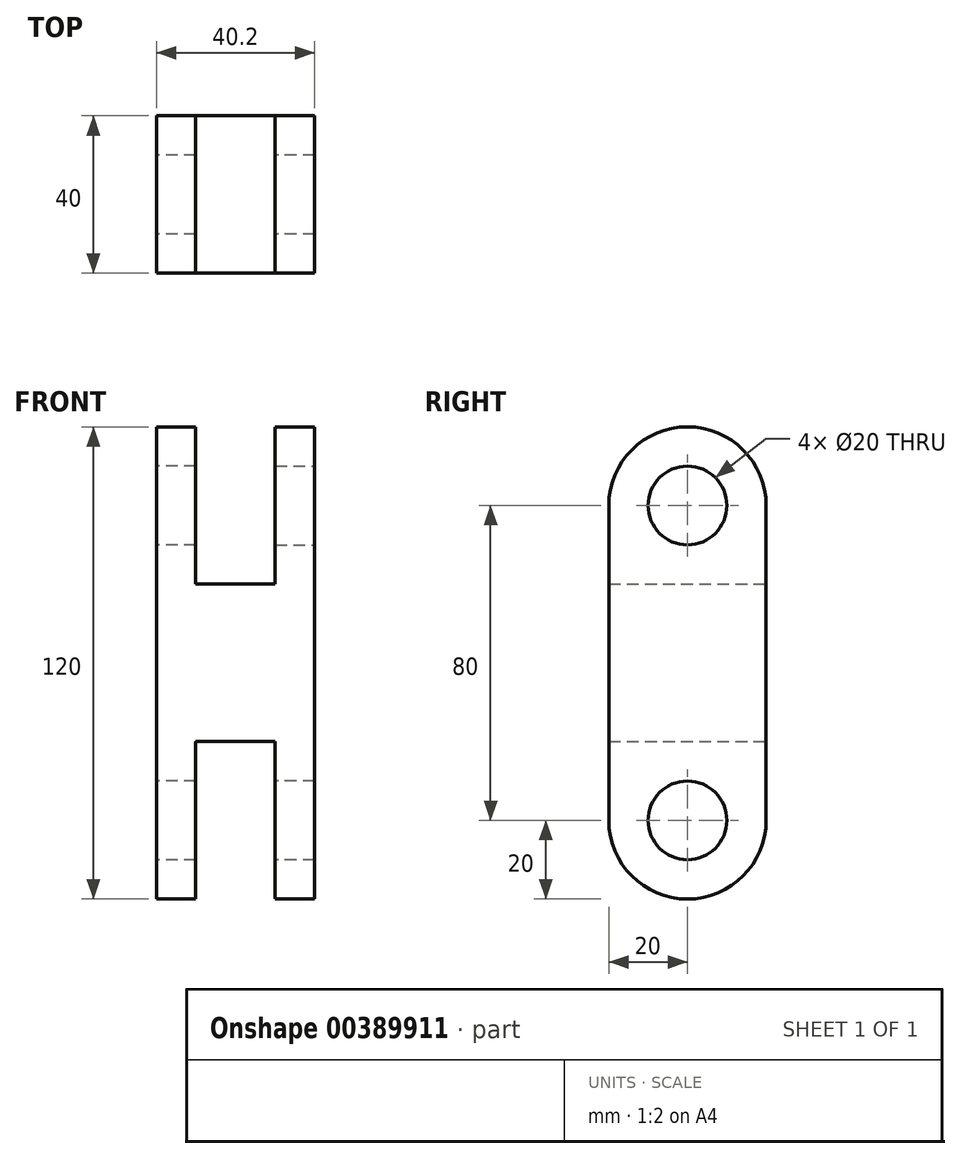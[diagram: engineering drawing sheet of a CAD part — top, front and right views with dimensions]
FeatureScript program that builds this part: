
annotation { "Feature Type Name" : "Feature", "Feature Type Description" : "" }
export const myFeature = defineFeature(function(context is Context, id is Id, definition is map)
    precondition{}
    {
        {
            var Q0;
            Q0=qCreatedBy(makeId("Right.planeOp"),FACE);
            var sketch = newSketch(context, id + "F0", { "sketchPlane" : qUnion([Q0])});
            skLineSegment(sketch, "E0.bottom", {"start": v(-20, 40) * mm, "end": v(20, 40) * mm});
            skLineSegment(sketch, "E0.top", {"start": v(-20, -40) * mm, "end": v(20, -40) * mm});
            skLineSegment(sketch, "E0.left", {"start": v(-20, 40) * mm, "end": v(-20, -40) * mm});
            skLineSegment(sketch, "E0.right", {"start": v(20, 40) * mm, "end": v(20, -40) * mm});
            skPoint(sketch, "E0.middle", {"position": v(0, 0) * mm});
            skSolve(sketch);
        }
        {
            var Q0;
            Q0 = qSketchRegion(id + "F0", true);
            extrude(context, id + "F1", {"entities" : qUnion([Q0]), "depth" : 20.1 * mm});
        }
        {
            var Q0;
            Q0=makeQuery(id+"F1.opExtrude","CAP_FACE",FACE,{"disambiguationData":[OSD([sQuery(id+"F0.wireOp",EDGE,"E0.bottom"),sQuery(id+"F0.wireOp",EDGE,"E0.top"),sQuery(id+"F0.wireOp",EDGE,"E0.left"),sQuery(id+"F0.wireOp",EDGE,"E0.right")])],"isStart":false});
            var sketch = newSketch(context, id + "F2", { "sketchPlane" : qUnion([Q0])});
            skLineSegment(sketch, "E1.bottom", {"start": v(-20, 40) * mm, "end": v(20, 40) * mm});
            skLineSegment(sketch, "E1.top", {"start": v(-20, 80) * mm, "end": v(20, 80) * mm});
            skLineSegment(sketch, "E1.left", {"start": v(-20, 40) * mm, "end": v(-20, 80) * mm});
            skLineSegment(sketch, "E1.right", {"start": v(20, 40) * mm, "end": v(20, 80) * mm});
            skSolve(sketch);
        }
        {
            var Q0;
            Q0 = qSketchRegion(id + "F2", true);
            extrude(context, id + "F3", {"entities" : qUnion([Q0]), "operationType" : NewBodyOperationType.ADD, "oppositeDirection" : true, "depth" : 10 * mm});
        }
        {
            var Q0;
            Q0=makeQuery(id+"F3.boolean.opBoolean","MERGE",FACE,{"derivedFrom":[makeQuery(id+"F1.opExtrude","CAP_FACE",FACE,{"disambiguationData":[OSD([sQuery(id+"F0.wireOp",EDGE,"E0.bottom"),sQuery(id+"F0.wireOp",EDGE,"E0.top"),sQuery(id+"F0.wireOp",EDGE,"E0.left"),sQuery(id+"F0.wireOp",EDGE,"E0.right")])],"isStart":false}),makeQuery(id+"F3.opExtrude","CAP_FACE",FACE,{"disambiguationData":[OSD([sQuery(id+"F2.wireOp",EDGE,"E1.bottom"),sQuery(id+"F2.wireOp",EDGE,"E1.top"),sQuery(id+"F2.wireOp",EDGE,"E1.left"),sQuery(id+"F2.wireOp",EDGE,"E1.right")])],"isStart":true})]});
            var sketch = newSketch(context, id + "F4", { "sketchPlane" : qUnion([Q0])});
            skLineSegment(sketch, "E2", {"start": v(0, 80) * mm, "end": v(0, 60) * mm, "construction": true});
            skCircle(sketch, "E3", {"center": v(0, 60) * mm, "radius": 10 * mm});
            skSolve(sketch);
        }
        {
            var Q0;
            Q0 = qSketchRegion(id + "F4", true);
            extrude(context, id + "F5", {"entities" : qUnion([Q0]), "operationType" : NewBodyOperationType.REMOVE, "oppositeDirection" : true, "depth" : 10.1 * mm});
        }
        {
            var Q0;
            Q0=makeQuery(id+"F1.opExtrude","SWEPT_BODY",BODY,{"disambiguationData":[OSD([sQuery(id+"F0.wireOp",EDGE,"E0.bottom"),sQuery(id+"F0.wireOp",EDGE,"E0.top"),sQuery(id+"F0.wireOp",EDGE,"E0.left"),sQuery(id+"F0.wireOp",EDGE,"E0.right")])]});
            var Q1;
            Q1=makeQuery(id+"F1.opExtrude","CAP_FACE",FACE,{"disambiguationData":[OSD([sQuery(id+"F0.wireOp",EDGE,"E0.bottom"),sQuery(id+"F0.wireOp",EDGE,"E0.top"),sQuery(id+"F0.wireOp",EDGE,"E0.left"),sQuery(id+"F0.wireOp",EDGE,"E0.right")])],"isStart":true});
            mirror(context, id + "F6", {"operationType" : NewBodyOperationType.ADD, "entities" : qUnion([Q0]), "mirrorPlane" : qUnion([Q1])});
        }
        {
            var Q0;
            Q0=makeQuery(id+"F3.opExtrude","SWEPT_EDGE",EDGE,{"disambiguationData":[OSD([sQuery(id+"F2.wireOp",EDGE,"E1.top"),sQuery(id+"F2.wireOp",EDGE,"E1.right")])]});
            var Q1;
            Q1=makeQuery(id+"F3.opExtrude","SWEPT_EDGE",EDGE,{"disambiguationData":[OSD([sQuery(id+"F2.wireOp",EDGE,"E1.top"),sQuery(id+"F2.wireOp",EDGE,"E1.left")])]});
            var Q2;
            Q2=makeQuery(id+"F6.opPattern","COPY",EDGE,{"derivedFrom":makeQuery(id+"F3.opExtrude","SWEPT_EDGE",EDGE,{"disambiguationData":[OSD([sQuery(id+"F2.wireOp",EDGE,"E1.top"),sQuery(id+"F2.wireOp",EDGE,"E1.right")])]}),"instanceName":"1"});
            var Q3;
            Q3=makeQuery(id+"F6.opPattern","COPY",EDGE,{"derivedFrom":makeQuery(id+"F3.opExtrude","SWEPT_EDGE",EDGE,{"disambiguationData":[OSD([sQuery(id+"F2.wireOp",EDGE,"E1.top"),sQuery(id+"F2.wireOp",EDGE,"E1.left")])]}),"instanceName":"1"});
            fillet(context, id + "F7", {"entities" : qUnion([Q0, Q1, Q2, Q3]), "radius" : 20 * mm, "tangentPropagation" : true, "allowEdgeOverflow" : false});
        }
        {
            var Q0;
            Q0=makeQuery(id+"F6.opPattern","COPY",FACE,{"derivedFrom":makeQuery(id+"F3.boolean.opBoolean","MERGE",FACE,{"derivedFrom":[makeQuery(id+"F1.opExtrude","CAP_FACE",FACE,{"disambiguationData":[OSD([sQuery(id+"F0.wireOp",EDGE,"E0.bottom"),sQuery(id+"F0.wireOp",EDGE,"E0.top"),sQuery(id+"F0.wireOp",EDGE,"E0.left"),sQuery(id+"F0.wireOp",EDGE,"E0.right")])],"isStart":false}),makeQuery(id+"F3.opExtrude","CAP_FACE",FACE,{"disambiguationData":[OSD([sQuery(id+"F2.wireOp",EDGE,"E1.bottom"),sQuery(id+"F2.wireOp",EDGE,"E1.top"),sQuery(id+"F2.wireOp",EDGE,"E1.left"),sQuery(id+"F2.wireOp",EDGE,"E1.right")])],"isStart":true})]}),"instanceName":"1"});
            var sketch = newSketch(context, id + "F8", { "sketchPlane" : qUnion([Q0])});
            skLineSegment(sketch, "E4", {"start": v(0, -40) * mm, "end": v(0, -20) * mm, "construction": true});
            skPoint(sketch, "E4.endSnap0", {"position": v(0, -40) * mm});
            skCircle(sketch, "E5", {"center": v(0, -20) * mm, "radius": 10 * mm});
            skSolve(sketch);
        }
        {
            var Q0;
            Q0=makeQuery(id+"F8.imprint","IMPRINT",FACE,{"disambiguationData":[TD([[makeQuery(id+"F8.imprint","IMPRINT",EDGE,{"derivedFrom":sQuery(id+"F8.wireOp",EDGE,"E5")}),1.0]])]});
            extrude(context, id + "F9", {"entities" : qUnion([Q0]), "operationType" : NewBodyOperationType.REMOVE, "oppositeDirection" : true, "depth" : 80 * mm});
        }
        {
            var Q0;
            {var subQ0=makeQuery(id+"F3.boolean.opBoolean","MERGE",FACE,{"derivedFrom":[makeQuery(id+"F1.opExtrude","SWEPT_FACE",FACE,{"disambiguationData":[OSD([sQuery(id+"F0.wireOp",EDGE,"E0.right")])]}),makeQuery(id+"F3.opExtrude","SWEPT_FACE",FACE,{"disambiguationData":[OSD([sQuery(id+"F2.wireOp",EDGE,"E1.right")])]})]});Q0=makeQuery(id+"F6.boolean.opBoolean","MERGE",FACE,{"derivedFrom":[subQ0,makeQuery(id+"F6.opPattern","COPY",FACE,{"derivedFrom":subQ0,"instanceName":"1"})]});}
            var sketch = newSketch(context, id + "F10", { "sketchPlane" : qUnion([Q0])});
            skLineSegment(sketch, "E6.bottom", {"start": v(-10.1, -40) * mm, "end": v(10.1, -40) * mm});
            skLineSegment(sketch, "E6.top", {"start": v(-10.1, 0) * mm, "end": v(10.1, 0) * mm});
            skLineSegment(sketch, "E6.left", {"start": v(-10.1, -40) * mm, "end": v(-10.1, 0) * mm});
            skLineSegment(sketch, "E6.right", {"start": v(10.1, -40) * mm, "end": v(10.1, 0) * mm});
            skSolve(sketch);
        }
        {
            var Q0;
            Q0 = qSketchRegion(id + "F10", true);
            var Q1;
            {var subQ0=makeQuery(id+"F3.boolean.opBoolean","MERGE",FACE,{"derivedFrom":[makeQuery(id+"F1.opExtrude","SWEPT_FACE",FACE,{"disambiguationData":[OSD([sQuery(id+"F0.wireOp",EDGE,"E0.left")])]}),makeQuery(id+"F3.opExtrude","SWEPT_FACE",FACE,{"disambiguationData":[OSD([sQuery(id+"F2.wireOp",EDGE,"E1.left")])]})]});Q1=makeQuery(id+"F6.boolean.opBoolean","MERGE",FACE,{"derivedFrom":[subQ0,makeQuery(id+"F6.opPattern","COPY",FACE,{"derivedFrom":subQ0,"instanceName":"1"})]});}
            extrude(context, id + "F11", {"entities" : qUnion([Q0]), "operationType" : NewBodyOperationType.REMOVE, "endBound" : BoundingType.UP_TO_SURFACE, "oppositeDirection" : true, "endBoundEntityFace" : qUnion([Q1]), "depth" : 25 * mm});
        }
        {
            var Q0;
            {var subQ0=sQuery(id+"F0.wireOp",EDGE,"E0.top");var subQ2=sQuery(id+"F0.wireOp",EDGE,"E0.right");var subQ6=makeQuery(id+"F1.opExtrude","SWEPT_EDGE",EDGE,{"disambiguationData":[OSD([subQ0,subQ2])]});Q0=makeQuery(id+"F11.boolean.opBoolean","SPLIT",EDGE,{"disambiguationData":[TD([makeQuery(id+"F11.opExtrude","SWEPT_FACE",FACE,{"disambiguationData":[OSD([sQuery(id+"F10.wireOp",EDGE,"E6.right")])]})])],"derivedFrom":makeQuery(id+"F6.boolean.opBoolean","MERGE",EDGE,{"derivedFrom":[subQ6,makeQuery(id+"F6.opPattern","COPY",EDGE,{"derivedFrom":subQ6,"instanceName":"1"})]})});}
            var Q1;
            {var subQ0=sQuery(id+"F0.wireOp",EDGE,"E0.top");var subQ2=sQuery(id+"F0.wireOp",EDGE,"E0.left");var subQ6=makeQuery(id+"F1.opExtrude","SWEPT_EDGE",EDGE,{"disambiguationData":[OSD([subQ0,subQ2])]});Q1=makeQuery(id+"F11.boolean.opBoolean","SPLIT",EDGE,{"disambiguationData":[TD([makeQuery(id+"F11.opExtrude","SWEPT_FACE",FACE,{"disambiguationData":[OSD([sQuery(id+"F10.wireOp",EDGE,"E6.right")])]})])],"derivedFrom":makeQuery(id+"F6.boolean.opBoolean","MERGE",EDGE,{"derivedFrom":[subQ6,makeQuery(id+"F6.opPattern","COPY",EDGE,{"derivedFrom":subQ6,"instanceName":"1"})]})});}
            var Q2;
            {var subQ1=sQuery(id+"F0.wireOp",EDGE,"E0.right");var subQ2=sQuery(id+"F0.wireOp",EDGE,"E0.top");var subQ6=makeQuery(id+"F1.opExtrude","SWEPT_EDGE",EDGE,{"disambiguationData":[OSD([subQ2,subQ1])]});Q2=makeQuery(id+"F11.boolean.opBoolean","SPLIT",EDGE,{"disambiguationData":[TD([makeQuery(id+"F11.opExtrude","SWEPT_FACE",FACE,{"disambiguationData":[OSD([sQuery(id+"F10.wireOp",EDGE,"E6.left")])]})])],"derivedFrom":makeQuery(id+"F6.boolean.opBoolean","MERGE",EDGE,{"derivedFrom":[subQ6,makeQuery(id+"F6.opPattern","COPY",EDGE,{"derivedFrom":subQ6,"instanceName":"1"})]})});}
            var Q3;
            {var subQ1=sQuery(id+"F0.wireOp",EDGE,"E0.left");var subQ2=sQuery(id+"F0.wireOp",EDGE,"E0.top");var subQ6=makeQuery(id+"F1.opExtrude","SWEPT_EDGE",EDGE,{"disambiguationData":[OSD([subQ2,subQ1])]});Q3=makeQuery(id+"F11.boolean.opBoolean","SPLIT",EDGE,{"disambiguationData":[TD([makeQuery(id+"F11.opExtrude","SWEPT_FACE",FACE,{"disambiguationData":[OSD([sQuery(id+"F10.wireOp",EDGE,"E6.left")])]})])],"derivedFrom":makeQuery(id+"F6.boolean.opBoolean","MERGE",EDGE,{"derivedFrom":[subQ6,makeQuery(id+"F6.opPattern","COPY",EDGE,{"derivedFrom":subQ6,"instanceName":"1"})]})});}
            fillet(context, id + "F12", {"entities" : qUnion([Q0, Q1, Q2, Q3]), "radius" : 20 * mm, "tangentPropagation" : true, "allowEdgeOverflow" : false});
        }
    });
